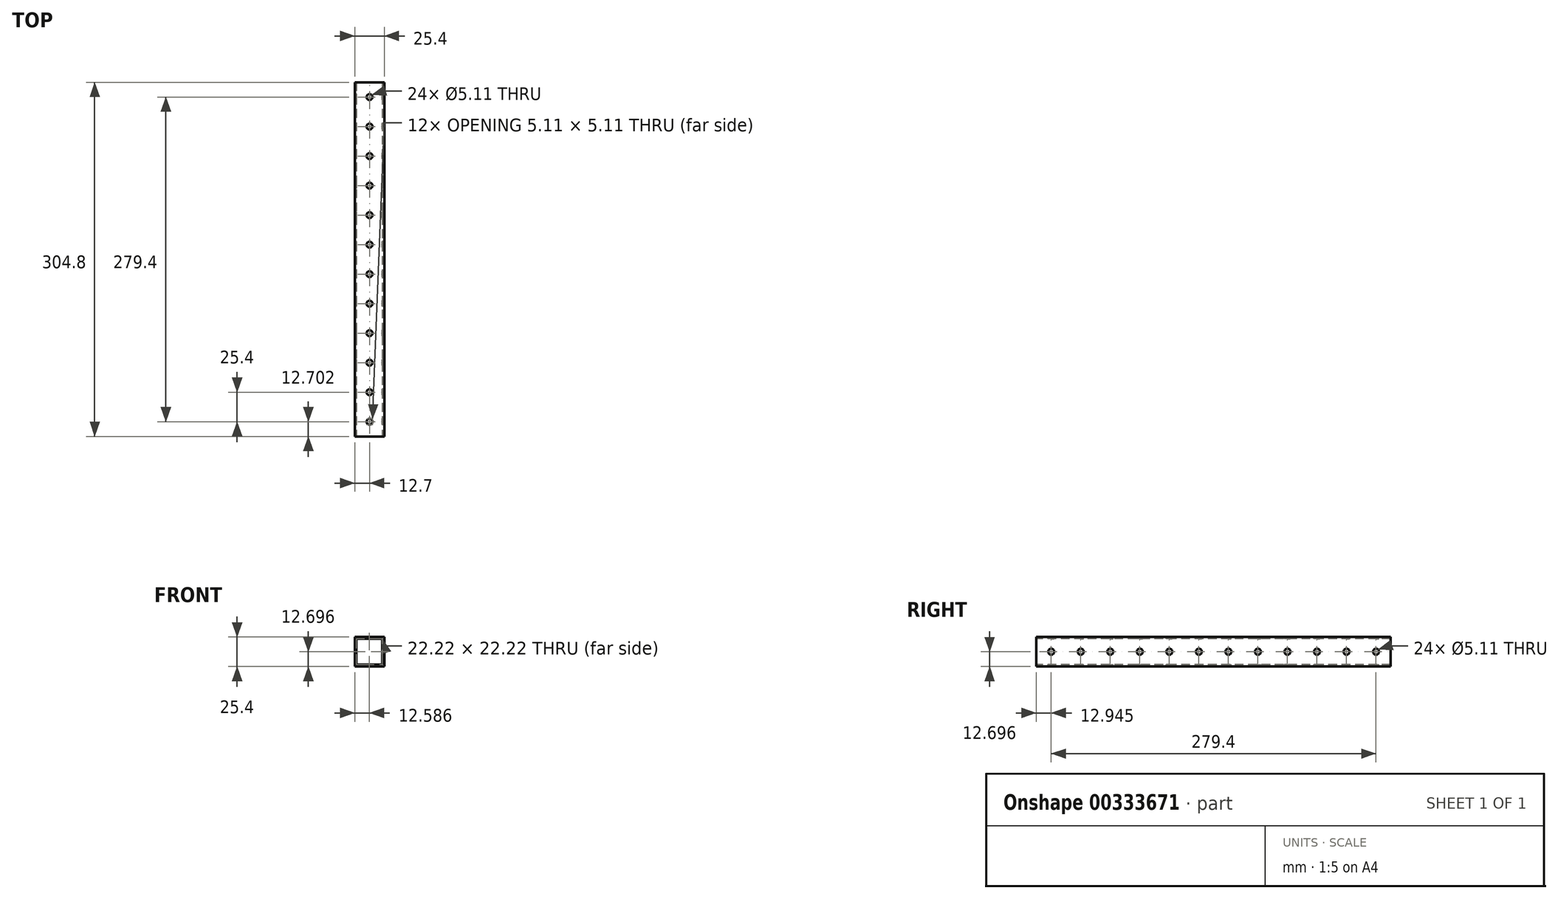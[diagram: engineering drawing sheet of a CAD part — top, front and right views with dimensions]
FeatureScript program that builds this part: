
annotation { "Feature Type Name" : "Feature", "Feature Type Description" : "" }
export const myFeature = defineFeature(function(context is Context, id is Id, definition is map)
    precondition{}
    {
        {
            var Q0;
            Q0=qCreatedBy(makeId("Right.planeOp"),FACE);
            var sketch = newSketch(context, id + "F0", { "sketchPlane" : qUnion([Q0])});
            skLineSegment(sketch, "E0.bottom", {"start": v(-73.53, 30.22) * mm, "end": v(231.27, 30.22) * mm});
            skLineSegment(sketch, "E0.top", {"start": v(-73.53, 4.82) * mm, "end": v(231.27, 4.82) * mm});
            skLineSegment(sketch, "E0.left", {"start": v(-73.53, 30.22) * mm, "end": v(-73.53, 4.82) * mm});
            skLineSegment(sketch, "E0.right", {"start": v(231.27, 30.22) * mm, "end": v(231.27, 4.82) * mm});
            skSolve(sketch);
        }
        {
            var Q0;
            Q0=makeQuery(id+"F0.imprint","IMPRINT",FACE,{"disambiguationData":[TD([[makeQuery(id+"F0.imprint","IMPRINT",EDGE,{"derivedFrom":sQuery(id+"F0.wireOp",EDGE,"E0.bottom")}),-1.0]])]});
            extrude(context, id + "F1", {"entities" : qUnion([Q0]), "depth" : 25.4 * mm});
        }
        {
            var Q0;
            Q0=makeQuery(id+"F1.opExtrude","SWEPT_FACE",FACE,{"disambiguationData":[OSD([sQuery(id+"F0.wireOp",EDGE,"E0.left")])]});
            var sketch = newSketch(context, id + "F2", { "sketchPlane" : qUnion([Q0])});
            skLineSegment(sketch, "E1.bottom", {"start": v(1.47, 28.63) * mm, "end": v(23.7, 28.63) * mm});
            skLineSegment(sketch, "E1.top", {"start": v(1.47, 6.4) * mm, "end": v(23.7, 6.4) * mm});
            skLineSegment(sketch, "E1.left", {"start": v(1.47, 28.63) * mm, "end": v(1.47, 6.4) * mm});
            skLineSegment(sketch, "E1.right", {"start": v(23.7, 28.63) * mm, "end": v(23.7, 6.4) * mm});
            skPoint(sketch, "E1.middle", {"position": v(12.59, 17.52) * mm});
            skPoint(sketch, "E1.middle.positionSnap0", {"position": v(0, 17.52) * mm});
            skPoint(sketch, "E1.centerSnap0", {"position": v(0, 17.52) * mm});
            skSolve(sketch);
        }
        {
            var Q0;
            Q0=makeQuery(id+"F2.imprint","IMPRINT",FACE,{"disambiguationData":[TD([[makeQuery(id+"F2.imprint","IMPRINT",EDGE,{"derivedFrom":sQuery(id+"F2.wireOp",EDGE,"E1.bottom")}),-1.0]])]});
            extrude(context, id + "F3", {"entities" : qUnion([Q0]), "operationType" : NewBodyOperationType.REMOVE, "oppositeDirection" : true, "depth" : 304.8 * mm});
        }
        {
            var Q0;
            Q0=makeQuery(id+"F1.opExtrude","SWEPT_FACE",FACE,{"disambiguationData":[OSD([sQuery(id+"F0.wireOp",EDGE,"E0.bottom")])]});
            var sketch = newSketch(context, id + "F4", { "sketchPlane" : qUnion([Q0])});
            skCircle(sketch, "E2", {"center": v(12.7, -60.83) * mm, "radius": 2.55 * mm});
            skCircle(sketch, "E3.0.1.0", {"center": v(12.7, -35.43) * mm, "radius": 2.55 * mm});
            skCircle(sketch, "E3.0.2.0", {"center": v(12.7, -10.03) * mm, "radius": 2.55 * mm});
            skCircle(sketch, "E3.0.3.0", {"center": v(12.7, 15.37) * mm, "radius": 2.55 * mm});
            skCircle(sketch, "E3.0.4.0", {"center": v(12.7, 40.77) * mm, "radius": 2.55 * mm});
            skCircle(sketch, "E3.0.5.0", {"center": v(12.7, 66.17) * mm, "radius": 2.55 * mm});
            skCircle(sketch, "E3.0.6.0", {"center": v(12.7, 91.57) * mm, "radius": 2.55 * mm});
            skCircle(sketch, "E3.0.7.0", {"center": v(12.7, 116.97) * mm, "radius": 2.55 * mm});
            skCircle(sketch, "E3.0.8.0", {"center": v(12.7, 142.37) * mm, "radius": 2.55 * mm});
            skCircle(sketch, "E3.0.9.0", {"center": v(12.7, 167.77) * mm, "radius": 2.55 * mm});
            skCircle(sketch, "E3.0.10.0", {"center": v(12.7, 193.17) * mm, "radius": 2.55 * mm});
            skCircle(sketch, "E3.0.11.0", {"center": v(12.7, 218.57) * mm, "radius": 2.55 * mm});
            skLineSegment(sketch, "E3.direction1", {"start": v(12.7, -60.83) * mm, "end": v(38.1, -60.83) * mm, "construction": true});
            skLineSegment(sketch, "E3.direction2", {"start": v(12.7, -60.83) * mm, "end": v(12.7, -35.43) * mm, "construction": true});
            skSolve(sketch);
        }
        {
            var Q0;
            Q0=qSketchRegion(id+"F4",true);
            extrude(context, id + "F5", {"entities" : qUnion([Q0]), "operationType" : NewBodyOperationType.REMOVE, "oppositeDirection" : true, "depth" : 25.4 * mm});
        }
        {
            var Q0;
            Q0=makeQuery(id+"F1.opExtrude","CAP_FACE",FACE,{"disambiguationData":[OSD([sQuery(id+"F0.wireOp",EDGE,"E0.bottom"),sQuery(id+"F0.wireOp",EDGE,"E0.top"),sQuery(id+"F0.wireOp",EDGE,"E0.left"),sQuery(id+"F0.wireOp",EDGE,"E0.right")])],"isStart":true});
            var sketch = newSketch(context, id + "F6", { "sketchPlane" : qUnion([Q0])});
            skCircle(sketch, "E4", {"center": v(60.58, 17.52) * mm, "radius": 2.55 * mm});
            skCircle(sketch, "E5.1.0.0", {"center": v(35.18, 17.52) * mm, "radius": 2.55 * mm});
            skCircle(sketch, "E5.2.0.0", {"center": v(9.78, 17.52) * mm, "radius": 2.55 * mm});
            skCircle(sketch, "E5.3.0.0", {"center": v(-15.62, 17.52) * mm, "radius": 2.55 * mm});
            skCircle(sketch, "E5.4.0.0", {"center": v(-41.02, 17.52) * mm, "radius": 2.55 * mm});
            skCircle(sketch, "E5.5.0.0", {"center": v(-66.42, 17.52) * mm, "radius": 2.55 * mm});
            skCircle(sketch, "E5.6.0.0", {"center": v(-91.82, 17.52) * mm, "radius": 2.55 * mm});
            skCircle(sketch, "E5.7.0.0", {"center": v(-117.22, 17.52) * mm, "radius": 2.55 * mm});
            skCircle(sketch, "E5.8.0.0", {"center": v(-142.62, 17.52) * mm, "radius": 2.55 * mm});
            skCircle(sketch, "E5.9.0.0", {"center": v(-168.02, 17.52) * mm, "radius": 2.55 * mm});
            skCircle(sketch, "E5.10.0.0", {"center": v(-193.42, 17.52) * mm, "radius": 2.55 * mm});
            skCircle(sketch, "E5.11.0.0", {"center": v(-218.82, 17.52) * mm, "radius": 2.55 * mm});
            skLineSegment(sketch, "E5.direction1", {"start": v(60.58, 17.52) * mm, "end": v(35.18, 17.52) * mm, "construction": true});
            skSolve(sketch);
        }
        {
            var Q0;
            Q0=qSketchRegion(id+"F6",true);
            extrude(context, id + "F7", {"entities" : qUnion([Q0]), "operationType" : NewBodyOperationType.REMOVE, "oppositeDirection" : true, "depth" : 25.4 * mm});
        }
    });
